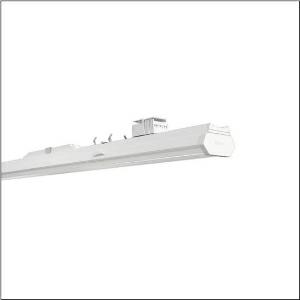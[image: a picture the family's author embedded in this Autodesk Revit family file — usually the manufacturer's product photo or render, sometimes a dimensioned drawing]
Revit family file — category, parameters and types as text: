
# Revit family: licross_r__11_protected_mo_51td11mn495g_5082
name_source: partatom
category: Lighting Fixtures
units: mm (PartAtom-declared; Revit-internal decimal feet)

## family parameters
Cut with Voids When Loaded = No
Host = Face
Light Source = No
Part Type = Normal
Room Calculation Point = No
Round Connector Dimension = Use Diameter
Shared = No

## types (1)
- --- (1 x LED, 9980 lm, 55.3 W, 4000K)
    Apparent Load = 55 VA
    CIE Flux Codes = 83 94 98 100 100
    Color Rendering = 80
    Color Temperature = 4000K
    Default Elevation = 1800 mm
    Description = Licross® 11 Protected MO, luminaire insert, of sheet steel, galvanised, coil coated, white, length: 1.500mm, width: 90mm, height: 101mm, LED rated luminous flux: 9.980lm, light colour: 840, control gear: ON/OFF Multilumen, with plug, 3-pole, with phase selection, mains connection: 220..240V, AC, 50/60Hz, rated input power: 55W, halogen-free wiring, primary light control with lens, of plastic, primary optical cover: cover, of PMMA, light emission: direct distribution, primary light characteristic: symmetric, protection rating (complete): IP54, insulation class (complete): insulation class I (protective earthing), certification: CE, ENEC, VDE, UKCA, protection symbol: D if used in an environment with non-conductive dust loads with corresponding accessories, impact resistance: IK06, permissible ambient temperature for indoor applications: -35..+40°C, corresponds to IFS (International Featured Standards) requirements for safety and quality in the food industry, reducing of maximum allowable ambient temperature of 5°C with ceiling mounting, LABS conformity tested according to VDMA 24364:2018-05, packaging unit: 1 piece
    Height = 92 mm
    Lamp = 1 x LED
    Lamp Light Flux = 9980 lm
    Lamp Power = 55.3 W
    Lamp count = 1
    Length = 1500 mm
    Luminous efficacy = 180 lm/W
    Manufacturer = Siteco
    ModVariant = No
    Model = 51TD11MN495G
    Mounting Place = Ceiling
    Mounting Type = Pendant
    Number of Poles = 1
    OnlyDefault = Yes
    Power Factor = 1
    Product Name = Licross® 11 Protected MO
    Product group = luminaire insert
    ProductGroupID = 902
    Protection Class = Protection class I
    Protection Degree = IP 54
    RLX_Detail_Level = 1
    RLX_Emergency_Light_Flux = 0 lm
    RLX_Emergency_Type = 0
    RLX_Emergency_Type_DB = No
    RlxData = <blob elided: 21857 chars, md5=c953a67d>
    Socket = socket
    Standby Power = 0 W
    System Light Flux = 9980 lm
    System Power = 55 W
    Type Comments = factory setting: luminous flux: 100 % | (A | C | E) | 126 mA
    Type Image = l_1256145.jpg
    URL = http://relux.com
    VarID = @adj_085792
    Voltage = 0 V
    Weight = 0.00 kg
    Width = 88 mm

## geometry (parser evidence)
native form markers: Blend x4, Sweep x10
no freeform markers — native parametric forms only
